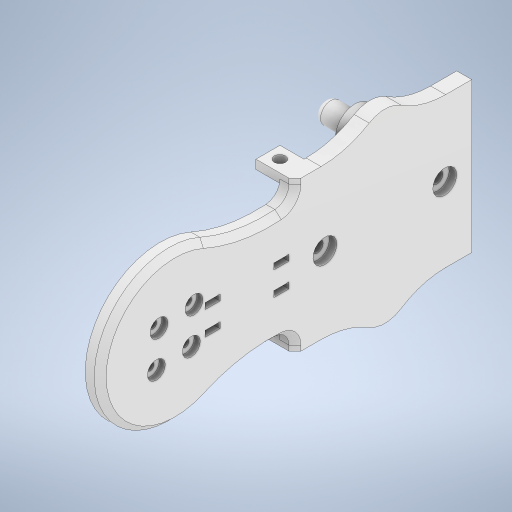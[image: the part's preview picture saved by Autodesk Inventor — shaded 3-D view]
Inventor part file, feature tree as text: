
AUTODESK INVENTOR PART (.ipt)
format: ipt  version: 2024.2 (Build 282272000, 272)  size: 530,432 bytes
history: native  units: in
note: dims shown in document units (in); Inventor stores cm internally (conversion verified against a paired STEP export)
features: extrude x10, sketch x5, fillet x5, mirror x1, chamfer x1
ambient origin geometry x8: Origin, YZ Plane, XZ Plane, XY Plane, X Axis, Y Axis, Z Axis, Center Point
bodies: Solid1 (feature_tree)
feature tree (22):
  sketch  "Sketch1"  dims[d0=0.15in d1=0.15in]
  extrude  "Extrusion1"  Depth=0.15in
  extrude  "Extrusion3"  Depth=0.3937in
  extrude  "Extrusion4"  Depth=0.3937in
  fillet  "Face Fillet1"
  fillet  "Face Fillet2"
  extrude  "Extrusion8"  Depth=1.9685in
  extrude  "Extrusion9"  Depth=0.3937in
  fillet  "Fillet2"  Radius=0.7874in
  extrude  "Extrusion10"  Depth=0.0197in
  fillet  "Fillet3"  Radius=0.1in
  extrude  "Extrusion11"  Depth=0.1969in TaperAngle=0.0deg
  extrude  "Extrusion12"  Depth=0.0197in
  extrude  "Extrusion13"  Depth=0.2756in
  extrude  "Extrusion15"  Depth=0.2756in
  mirror  "Mirror1"
  fillet  "Fillet4"  Radius=0.7874in
  chamfer  "Chamfer2"  Distance=0.7874in
  sketch  "Sketch8"  dims[d2=1.5748in d3=0.3937in]
  sketch  "Sketch9"  dims[d5=0.3543in d7=0.3937in]
  sketch  "Sketch10"  dims[d8=0.3937in d9=1.9685in]
  sketch  "Sketch12"  dims[d12=1.1811in d13=0.3937in d14=0.7874in d18=0.1in d19=0.1in d22=0.1969in d23=0.0in d30=0.8268in d31=0.2756in d32=0.2756in d33=0.7874in d34=0.7874in d36=0.5906in d37=0.0in d38=0.1181in d39=0.1969in d40=0.0in d48=0.5906in d55=0.5906in d56=0.3425in d57=0.3425in d58=0.5906in d66=0.1969in d67=0.1969in d88=0.1181in d91=0.3in d93=0.35in d95=45.0deg d96=0.2362in d97=0.2362in d98=0.2362in d99=0.2362in d100=0.0787in d101=0.0in d102=0.1181in d104=0.2362in d105=1.1811in d106=0.0787in d107=0.0in d108=0.0787in d115=0.1969in d117=0.1969in d118=0.0787in d119=0.0787in d120=0.0in d121=0.2362in d129=0.0787in d130=0.1181in d132=0.0787in d133=0.0787in d134=0.315in d135=0.315in d136=0.0984in d137=0.0in d138=0.2362in d139=0.0394in d140=0.0in d143=0.315in d144=0.0in d150=0.315in d151=0.1181in d152=0.15in d153=0.1575in d154=0.1575in d155=0.315in d156=0.0in d157=0.0787in d158=0.0787in d159=0.0787in d160=45.0deg d54=0.0in d89=0.0197in d90=0.0344in d92=0.0344in]
